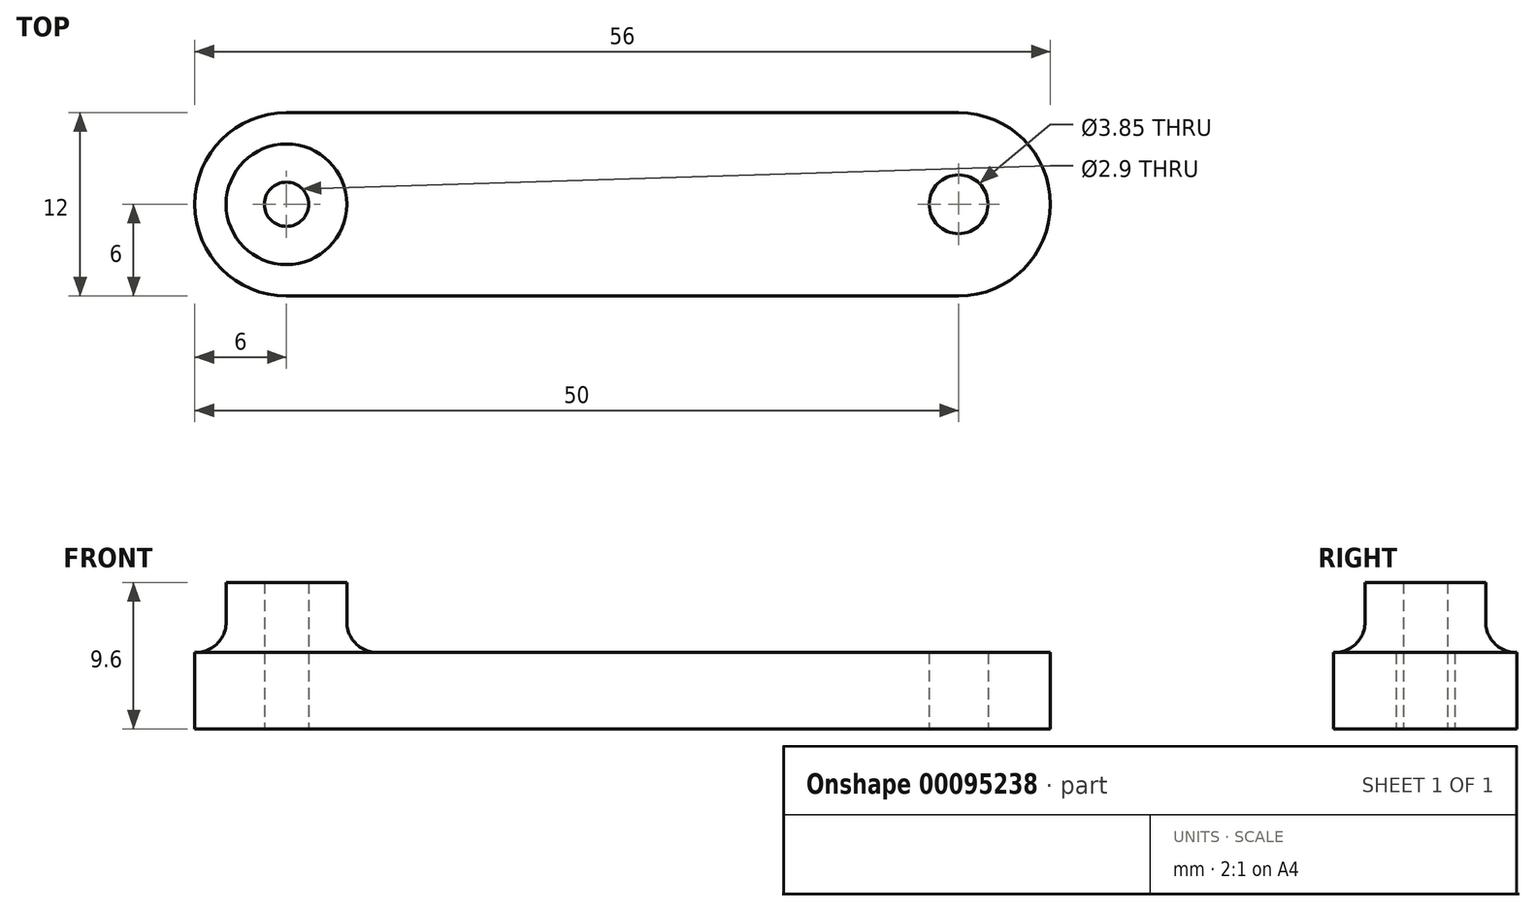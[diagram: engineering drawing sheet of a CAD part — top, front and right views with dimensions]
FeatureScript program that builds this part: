
annotation { "Feature Type Name" : "Feature", "Feature Type Description" : "" }
export const myFeature = defineFeature(function(context is Context, id is Id, definition is map)
    precondition{}
    {
        {
            var Q0;
            Q0=qCreatedBy(makeId("Top.planeOp"),FACE);
            var sketch = newSketch(context, id + "F0", { "sketchPlane" : qUnion([Q0])});
            skArc(sketch, "E0", {"start": v(0, -6) * mm, "mid": v(6, 0) * mm, "end": v(0, 6) * mm});
            skLineSegment(sketch, "E1", {"start": v(0, 6) * mm, "end": v(-44, 6) * mm});
            skLineSegment(sketch, "E2", {"start": v(0, -6) * mm, "end": v(-44, -6) * mm});
            skArc(sketch, "E3", {"start": v(-44, 6) * mm, "mid": v(-50, 0) * mm, "end": v(-44, -6) * mm});
            skCircle(sketch, "E4", {"center": v(-44, 0) * mm, "radius": 1.93 * mm});
            skCircle(sketch, "E5", {"center": v(0, 0) * mm, "radius": 1.93 * mm});
            skSolve(sketch);
        }
        {
            var Q0;
            Q0 = qSketchRegion(id + "F0", true);
            extrude(context, id + "F1", {"entities" : qUnion([Q0]), "depth" : 5 * mm});
        }
        {
            var Q0;
            Q0=makeQuery(id+"F1.opExtrude","CAP_FACE",FACE,{"disambiguationData":[OSD([sQuery(id+"F0.wireOp",EDGE,"E0"),sQuery(id+"F0.wireOp",EDGE,"E1"),sQuery(id+"F0.wireOp",EDGE,"E2"),sQuery(id+"F0.wireOp",EDGE,"E3"),sQuery(id+"F0.wireOp",EDGE,"E4"),sQuery(id+"F0.wireOp",EDGE,"E5")])],"isStart":false});
            var sketch = newSketch(context, id + "F2", { "sketchPlane" : qUnion([Q0])});
            skCircle(sketch, "E6", {"center": v(-44, 0) * mm, "radius": 1.45 * mm});
            skCircle(sketch, "E7", {"center": v(-44, 0) * mm, "radius": 3.95 * mm});
            skSolve(sketch);
        }
        {
            var Q0;
            Q0 = qSketchRegion(id + "F2", true);
            var Q1;
            Q1=makeQuery(id+"F1.opExtrude","CAP_FACE",FACE,{"disambiguationData":[OSD([sQuery(id+"F0.wireOp",EDGE,"E0"),sQuery(id+"F0.wireOp",EDGE,"E1"),sQuery(id+"F0.wireOp",EDGE,"E2"),sQuery(id+"F0.wireOp",EDGE,"E3"),sQuery(id+"F0.wireOp",EDGE,"E4"),sQuery(id+"F0.wireOp",EDGE,"E5")])],"isStart":true});
            extrude(context, id + "F3", {"entities" : qUnion([Q0]), "operationType" : NewBodyOperationType.ADD, "depth" : 4.6 * mm, "hasSecondDirection" : true, "secondDirectionBound" : SecondDirectionBoundingType.UP_TO_SURFACE, "secondDirectionOppositeDirection" : true, "secondDirectionBoundEntityFace" : qUnion([Q1]), "secondDirectionDepth" : 25 * mm});
        }
        {
            var Q0;
            Q0=makeQuery(id+"F3.boolean.opBoolean","INTERSECT",EDGE,{"derivedFrom":[makeQuery(id+"F1.opExtrude","CAP_FACE",FACE,{"disambiguationData":[OSD([sQuery(id+"F0.wireOp",EDGE,"E0"),sQuery(id+"F0.wireOp",EDGE,"E1"),sQuery(id+"F0.wireOp",EDGE,"E2"),sQuery(id+"F0.wireOp",EDGE,"E3"),sQuery(id+"F0.wireOp",EDGE,"E4"),sQuery(id+"F0.wireOp",EDGE,"E5")])],"isStart":false}),makeQuery(id+"F3.opExtrude","SWEPT_FACE",FACE,{"disambiguationData":[OSD([sQuery(id+"F2.wireOp",EDGE,"E7")])]})]});
            fillet(context, id + "F4", {"entities" : qUnion([Q0]), "radius" : 2 * mm, "tangentPropagation" : true, "allowEdgeOverflow" : false});
        }
    });
